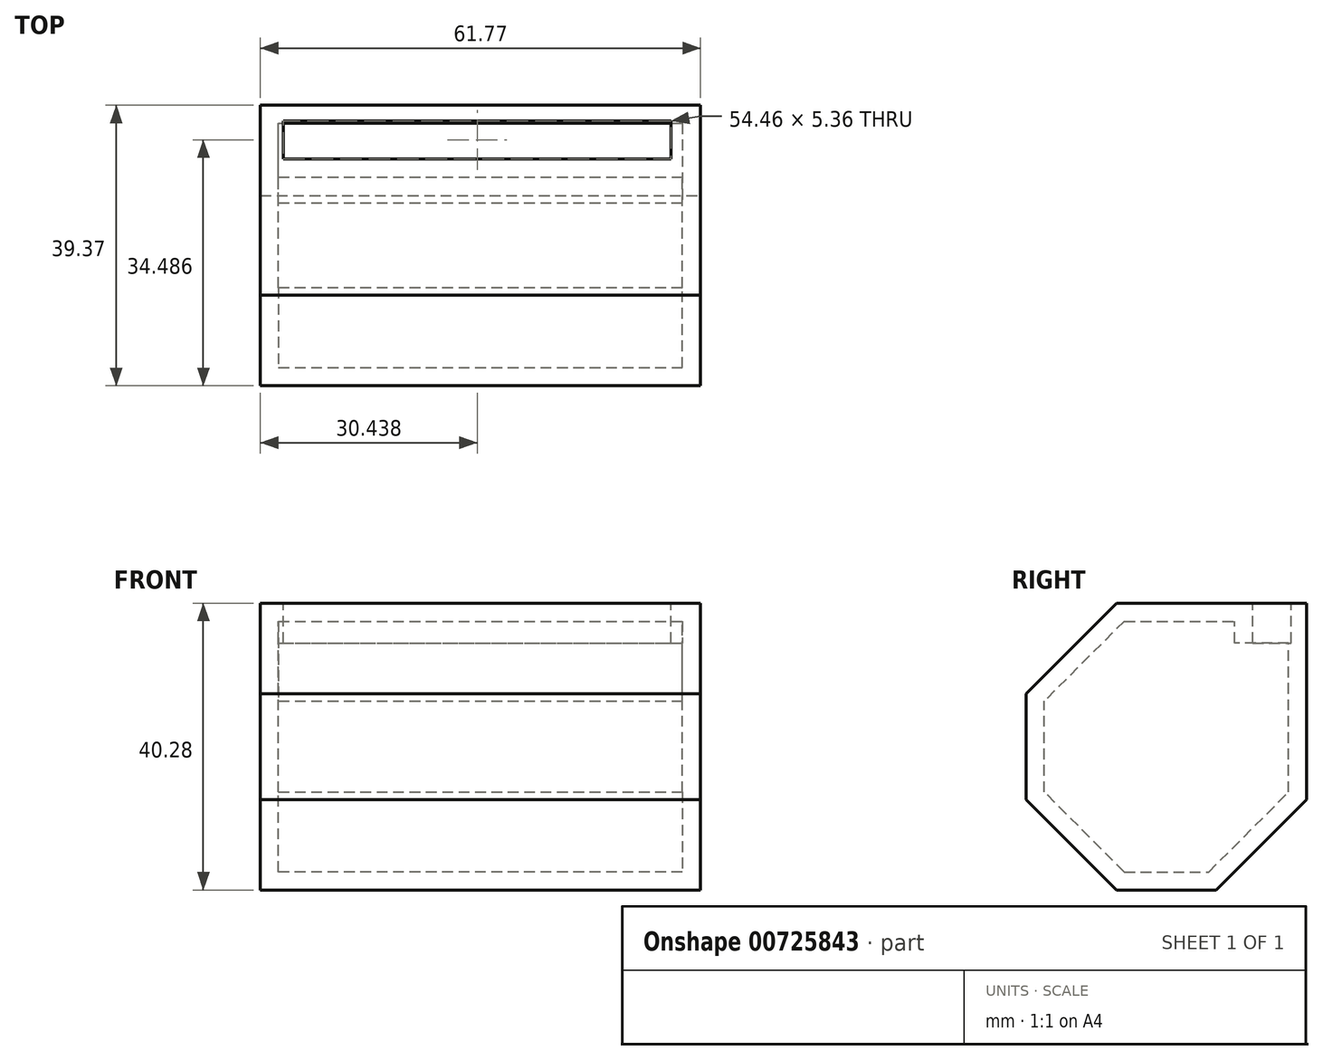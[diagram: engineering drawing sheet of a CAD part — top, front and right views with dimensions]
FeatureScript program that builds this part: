
annotation { "Feature Type Name" : "Feature", "Feature Type Description" : "" }
export const myFeature = defineFeature(function(context is Context, id is Id, definition is map)
    precondition{}
    {
        {
            var Q0;
            Q0=qCreatedBy(makeId("Front.planeOp"),FACE);
            var sketch = newSketch(context, id + "F0", { "sketchPlane" : qUnion([Q0])});
            skLineSegment(sketch, "E0.bottom", {"start": v(-33.88, -13.2) * mm, "end": v(27.9, -13.2) * mm});
            skLineSegment(sketch, "E0.top", {"start": v(-33.88, 27.08) * mm, "end": v(27.9, 27.08) * mm});
            skLineSegment(sketch, "E0.left", {"start": v(-33.88, -13.2) * mm, "end": v(-33.88, 27.08) * mm});
            skLineSegment(sketch, "E0.right", {"start": v(27.9, -13.2) * mm, "end": v(27.9, 27.08) * mm});
            skLineSegment(sketch, "E1.bottom", {"start": v(0, 27.08) * mm, "end": v(-9.93, 27.08) * mm});
            skLineSegment(sketch, "E1.top", {"start": v(0, 27.08) * mm, "end": v(-9.93, 27.08) * mm});
            skLineSegment(sketch, "E1.left", {"start": v(0, 27.08) * mm, "end": v(0, 27.08) * mm});
            skLineSegment(sketch, "E1.right", {"start": v(-9.93, 27.08) * mm, "end": v(-9.93, 27.08) * mm});
            skSolve(sketch);
        }
        {
            var Q0;
            Q0 = qSketchRegion(id + "F0", true);
            extrude(context, id + "F1", {"entities" : qUnion([Q0]), "depth" : 39.37 * mm, "offsetDistance" : 25.4 * mm});
        }
        {
            var Q0;
            Q0=makeQuery(id+"F1.opExtrude","CAP_EDGE",EDGE,{"disambiguationData":[OSD([sQuery(id+"F0.wireOp",EDGE,"E0.bottom")])],"isStart":false});
            var Q1;
            Q1=makeQuery(id+"F1.opExtrude","CAP_EDGE",EDGE,{"disambiguationData":[OSD([sQuery(id+"F0.wireOp",EDGE,"E0.top"),sQuery(id+"F0.wireOp",EDGE,"E1.top")])],"isStart":false});
            var Q2;
            Q2=makeQuery(id+"F1.opExtrude","CAP_EDGE",EDGE,{"disambiguationData":[OSD([sQuery(id+"F0.wireOp",EDGE,"E0.bottom")])],"isStart":true});
            chamfer(context, id + "F2", {"entities" : qUnion([Q0, Q1, Q2]), "width" : 12.7 * mm, "tangentPropagation" : true});
        }
        {
            var Q0;
            Q0=makeQuery(id+"F1.opExtrude","SWEPT_FACE",FACE,{"disambiguationData":[OSD([sQuery(id+"F0.wireOp",EDGE,"E0.top"),sQuery(id+"F0.wireOp",EDGE,"E1.top")])]});
            var sketch = newSketch(context, id + "F3", { "sketchPlane" : qUnion([Q0])});
            skLineSegment(sketch, "E2.bottom", {"start": v(-30.67, -7.57) * mm, "end": v(23.79, -7.57) * mm});
            skLineSegment(sketch, "E2.top", {"start": v(-30.67, -2.2) * mm, "end": v(23.79, -2.2) * mm});
            skLineSegment(sketch, "E2.left", {"start": v(-30.67, -7.57) * mm, "end": v(-30.67, -2.2) * mm});
            skLineSegment(sketch, "E2.right", {"start": v(23.79, -7.57) * mm, "end": v(23.79, -2.2) * mm});
            skSolve(sketch);
        }
        {
            var Q0;
            Q0=makeQuery(id+"F3.imprint","IMPRINT",FACE,{"disambiguationData":[TD([[makeQuery(id+"F3.imprint","IMPRINT",EDGE,{"derivedFrom":sQuery(id+"F3.wireOp",EDGE,"E2.bottom")}),1.0]])]});
            extrude(context, id + "F4", {"entities" : qUnion([Q0]), "operationType" : NewBodyOperationType.REMOVE, "oppositeDirection" : true, "depth" : 5.6 * mm, "offsetDistance" : 25.4 * mm});
        }
        {
            var Q0;
            Q0=makeQuery(id+"F4.boolean.opBoolean","COPY",FACE,{"derivedFrom":makeQuery(id+"F4.opExtrude","CAP_FACE",FACE,{"disambiguationData":[OSD([sQuery(id+"F3.wireOp",EDGE,"E2.bottom"),sQuery(id+"F3.wireOp",EDGE,"E2.top"),sQuery(id+"F3.wireOp",EDGE,"E2.left"),sQuery(id+"F3.wireOp",EDGE,"E2.right")])],"isStart":false})});
            shell(context, id + "F5", {"entities" : qUnion([Q0]), "thickness" : 2.54 * mm});
        }
    });
